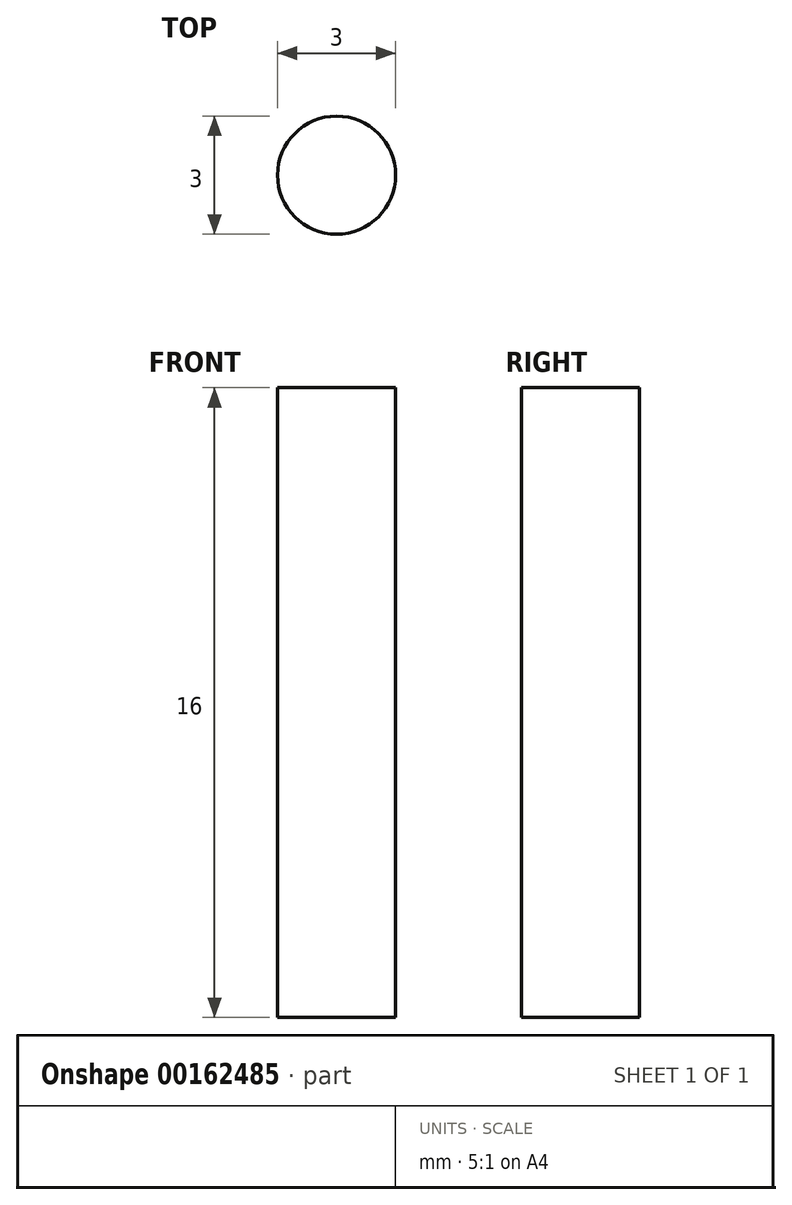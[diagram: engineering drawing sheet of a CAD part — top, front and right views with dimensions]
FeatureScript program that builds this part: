
annotation { "Feature Type Name" : "Feature", "Feature Type Description" : "" }
export const myFeature = defineFeature(function(context is Context, id is Id, definition is map)
    precondition{}
    {
        {
            var Q0;
            Q0=qCreatedBy(makeId("Top.planeOp"),FACE);
            var sketch = newSketch(context, id + "F0", { "sketchPlane" : qUnion([Q0])});
            skCircle(sketch, "E0", {"center": v(0, 0) * mm, "radius": 1.5 * mm});
            skSolve(sketch);
        }
        {
            var Q0;
            Q0 = qSketchRegion(id + "F0", true);
            extrude(context, id + "F1", {"entities" : qUnion([Q0]), "depth" : 16 * mm});
        }
    });
